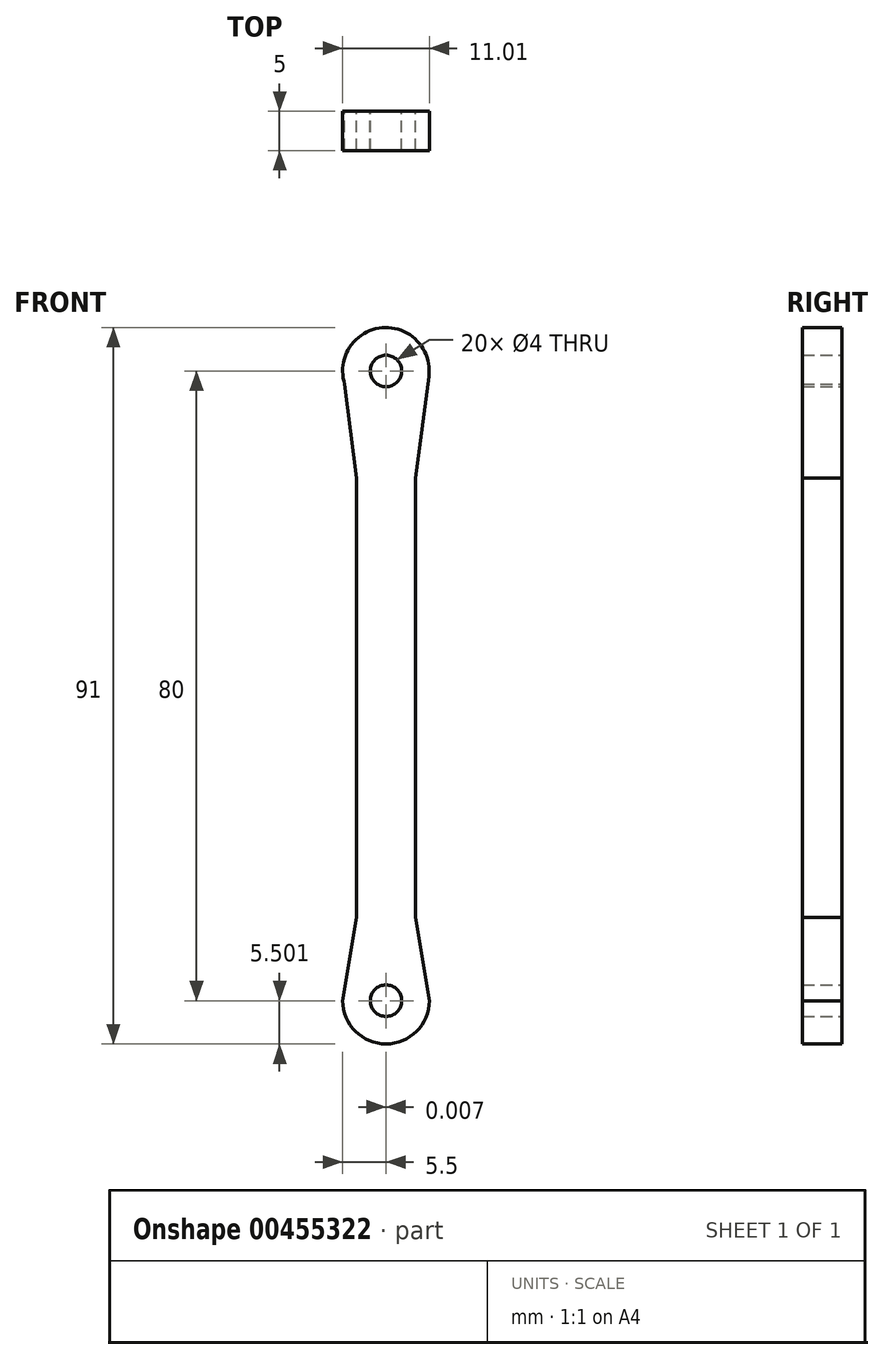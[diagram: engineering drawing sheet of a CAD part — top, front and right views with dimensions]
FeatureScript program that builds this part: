
annotation { "Feature Type Name" : "Feature", "Feature Type Description" : "" }
export const myFeature = defineFeature(function(context is Context, id is Id, definition is map)
    precondition{}
    {
        {
            var Q0;
            Q0=qCreatedBy(makeId("Front.planeOp"),FACE);
            var sketch = newSketch(context, id + "F0", { "sketchPlane" : qUnion([Q0])});
            skCircle(sketch, "E0", {"center": v(0, 44.75) * mm, "radius": 5.5 * mm});
            skArc(sketch, "E1", {"start": v(-5.5, -35.25) * mm, "mid": v(0, -40.75) * mm, "end": v(5.5, -35.25) * mm});
            skCircle(sketch, "E2", {"center": v(0, 44.75) * mm, "radius": 2 * mm});
            skCircle(sketch, "E3", {"center": v(0, -35.25) * mm, "radius": 2 * mm});
            skLineSegment(sketch, "E4", {"start": v(-3.76, 40.74) * mm, "end": v(-3.76, -35.25) * mm});
            skLineSegment(sketch, "E5", {"start": v(3.76, 40.74) * mm, "end": v(3.76, -35.25) * mm});
            skLineSegment(sketch, "E6", {"start": v(3.76, -35.25) * mm, "end": v(-5.5, -35.25) * mm});
            skLineSegment(sketch, "E7", {"start": v(-5.49, 45.13) * mm, "end": v(-3.76, 31.14) * mm});
            skLineSegment(sketch, "E8", {"start": v(-3.76, 31.14) * mm, "end": v(3.76, 31.14) * mm});
            skLineSegment(sketch, "E9", {"start": v(3.76, 31.14) * mm, "end": v(5.45, 44.04) * mm});
            skLineSegment(sketch, "E10", {"start": v(-5.5, -35.25) * mm, "end": v(-3.76, -24.67) * mm});
            skLineSegment(sketch, "E11", {"start": v(-3.76, -24.67) * mm, "end": v(5.5, -35.25) * mm});
            skLineSegment(sketch, "E12", {"start": v(5.5, -35.25) * mm, "end": v(3.76, -24.67) * mm});
            skSolve(sketch);
        }
        {
            var Q0;
            Q0 = qSketchRegion(id + "F0", true);
            extrude(context, id + "F1", {"entities" : qUnion([Q0]), "depth" : 5 * mm});
        }
    });
